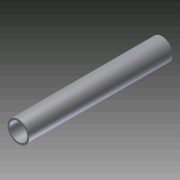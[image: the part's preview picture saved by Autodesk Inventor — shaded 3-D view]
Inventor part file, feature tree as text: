
AUTODESK INVENTOR PART (.ipt)
format: ipt  version: 2011 (Build 150239000, 239)  size: 69,120 bytes
history: native  units: in
note: dims shown in document units (in); Inventor stores cm internally (conversion verified against a paired STEP export)
features: extrude x1, sketch x1
ambient origin geometry x8: Origin, YZ Plane, XZ Plane, XY Plane, X Axis, Y Axis, Z Axis, Center Point
bodies: Solid1 (feature_tree)
feature tree (2):
  extrude  "Extrusion1"  Depth=0.48in
  sketch  "Sketch1"  dims[d0=0.397in d1=0.48in d2=3.181in d3=0.0in]
